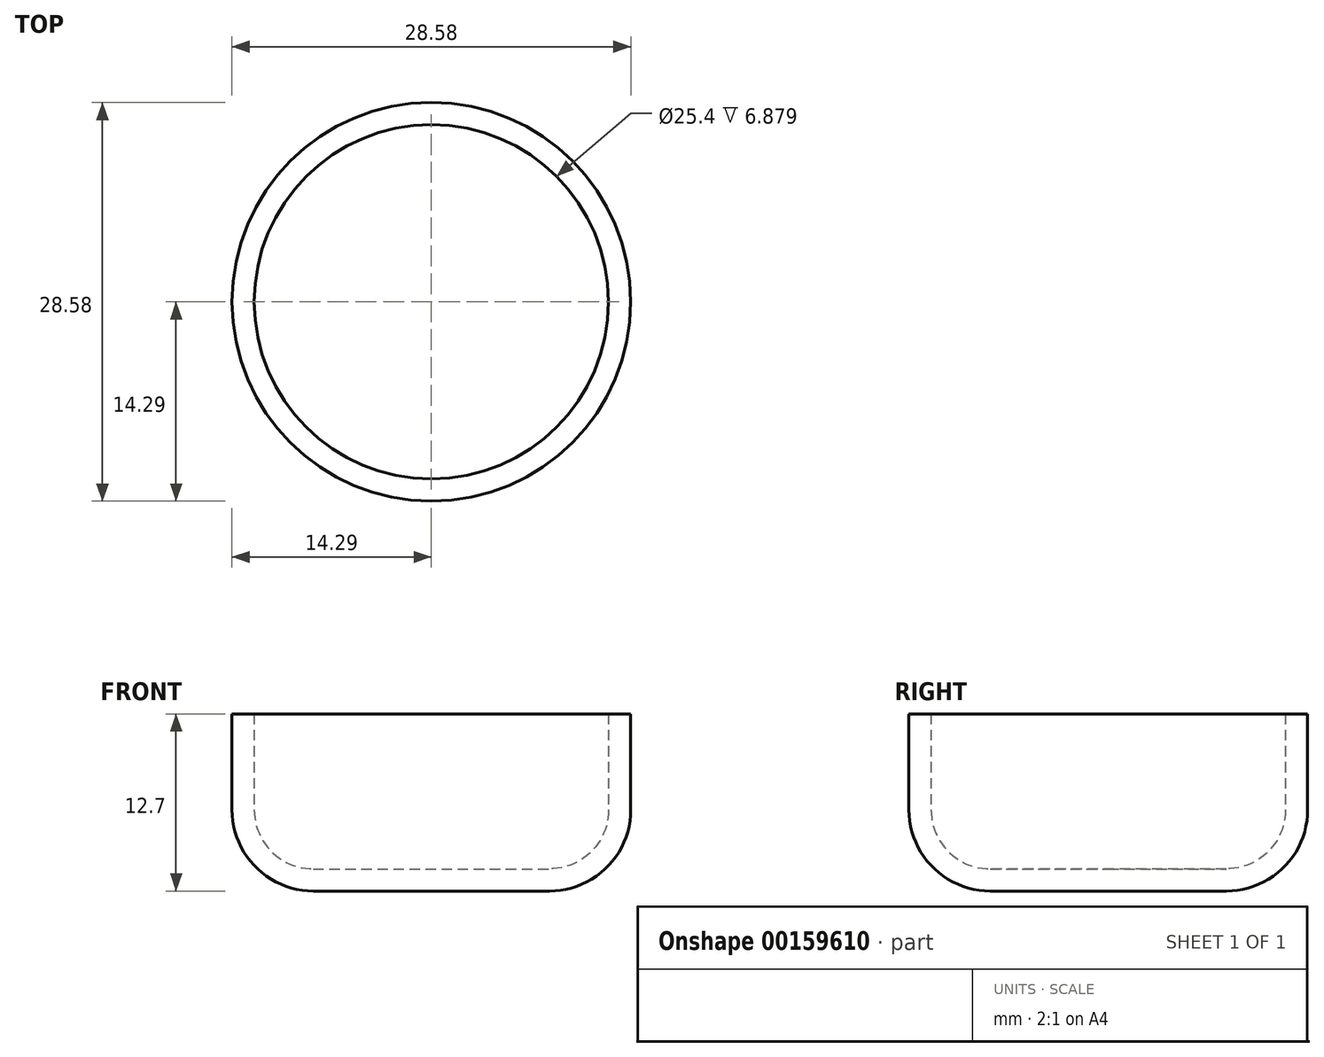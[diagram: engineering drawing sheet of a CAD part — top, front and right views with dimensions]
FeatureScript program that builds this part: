
annotation { "Feature Type Name" : "Feature", "Feature Type Description" : "" }
export const myFeature = defineFeature(function(context is Context, id is Id, definition is map)
    precondition{}
    {
        {
            var Q0;
            Q0=qCreatedBy(makeId("Front.planeOp"),FACE);
            var sketch = newSketch(context, id + "F0", { "sketchPlane" : qUnion([Q0])});
            skLineSegment(sketch, "E0", {"start": v(0, 0) * mm, "end": v(8.47, 0) * mm});
            skLineSegment(sketch, "E1", {"start": v(0, 0) * mm, "end": v(0, 12.7) * mm});
            skLineSegment(sketch, "E2", {"start": v(12.7, 12.7) * mm, "end": v(14.29, 12.7) * mm});
            skLineSegment(sketch, "E3.1", {"start": v(0, 1.59) * mm, "end": v(8.47, 1.59) * mm});
            skLineSegment(sketch, "E4", {"start": v(12.7, 12.7) * mm, "end": v(12.7, 5.82) * mm});
            skArc(sketch, "E5", {"start": v(8.47, 1.59) * mm, "mid": v(11.46, 2.83) * mm, "end": v(12.7, 5.82) * mm});
            skLineSegment(sketch, "E6", {"start": v(14.29, 12.7) * mm, "end": v(14.29, 5.82) * mm});
            skArc(sketch, "E7", {"start": v(8.47, 0) * mm, "mid": v(12.58, 1.7) * mm, "end": v(14.29, 5.82) * mm});
            skArc(sketch, "E8", {"start": v(0, 4.76) * mm, "mid": v(2.25, 3.83) * mm, "end": v(3.18, 1.59) * mm});
            skSolve(sketch);
        }
        {
            var Q0;
            {var subQ2=sQuery(id+"F0.wireOp",EDGE,"E0");Q0=makeQuery(id+"F0.imprint","IMPRINT",FACE,{"disambiguationData":[TD([[makeQuery(id+"F0.imprint","IMPRINT",EDGE,{"derivedFrom":subQ2}),1.0]])]});}
            var Q1;
            {var subQ3=sQuery(id+"F0.wireOp",EDGE,"E8");Q1=makeQuery(id+"F0.imprint","IMPRINT",FACE,{"disambiguationData":[TD([[makeQuery(id+"F0.imprint","IMPRINT",EDGE,{"derivedFrom":subQ3}),-1.0]])]});}
            var Q2;
            Q2=sQuery(id+"F0.wireOp",EDGE,"E1");
            revolve(context, id + "F1", {"entities" : qUnion([Q0, Q1]), "axis" : qUnion([Q2]), "revolveType" : RevolveType.FULL});
        }
    });
